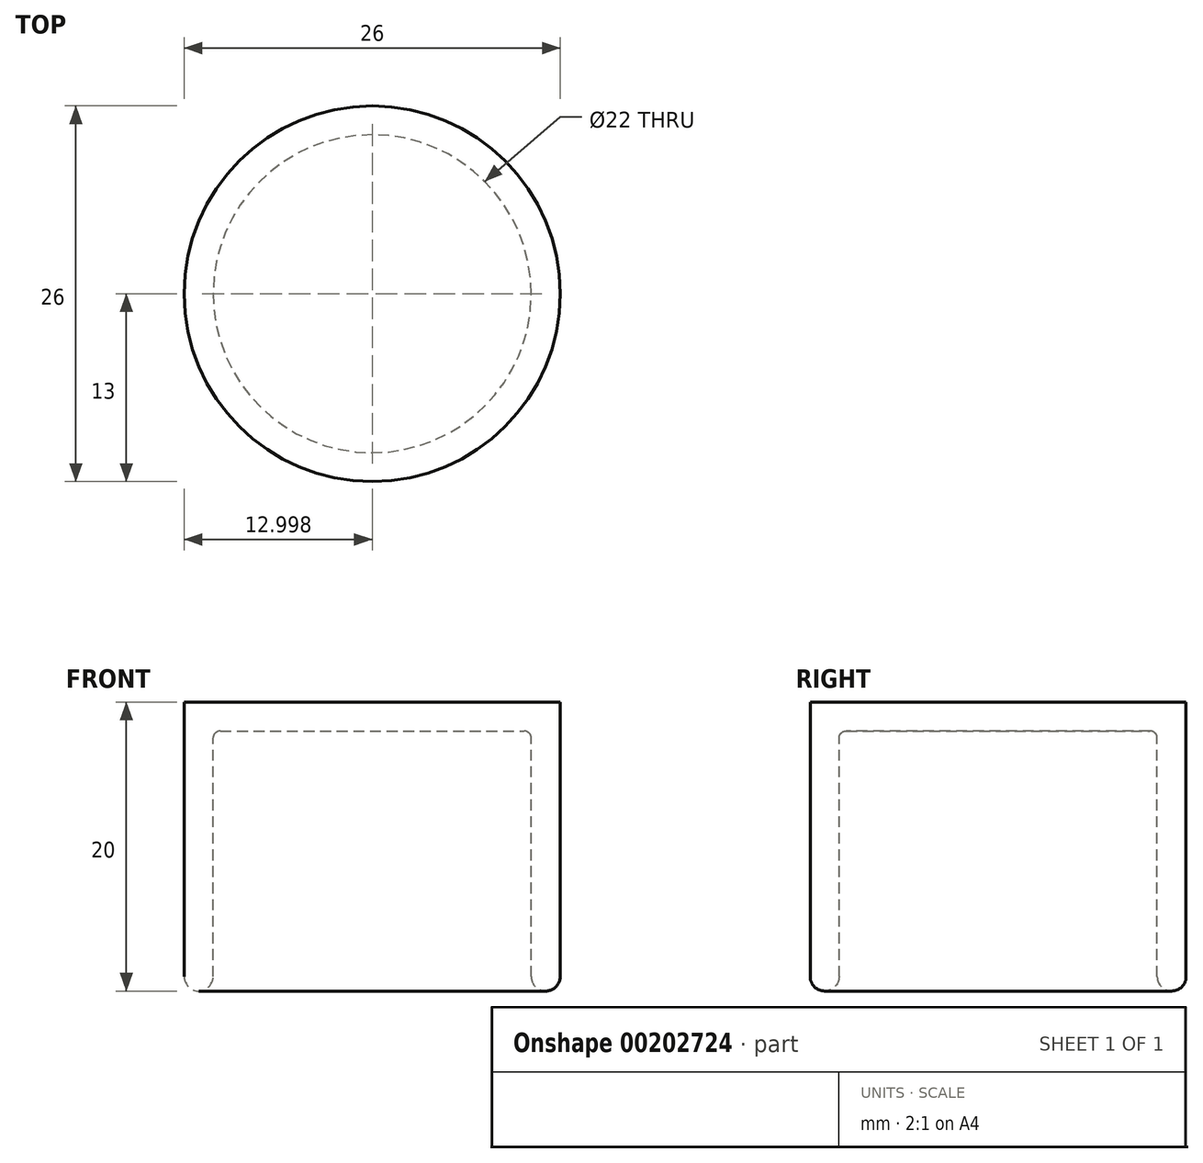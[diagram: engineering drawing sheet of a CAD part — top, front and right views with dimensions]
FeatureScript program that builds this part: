
annotation { "Feature Type Name" : "Feature", "Feature Type Description" : "" }
export const myFeature = defineFeature(function(context is Context, id is Id, definition is map)
    precondition{}
    {
        {
            var Q0;
            Q0=qCreatedBy(makeId("Front.planeOp"),FACE);
            var sketch = newSketch(context, id + "F0", { "sketchPlane" : qUnion([Q0])});
            skLineSegment(sketch, "E0.bottom", {"start": v(18.54, 12.93) * mm, "end": v(31.54, 12.93) * mm});
            skLineSegment(sketch, "E0.top", {"start": v(18.54, -7.07) * mm, "end": v(20.54, -7.07) * mm});
            skLineSegment(sketch, "E0.left", {"start": v(18.54, 12.93) * mm, "end": v(18.54, -7.07) * mm});
            skLineSegment(sketch, "E0.right", {"start": v(31.54, 12.93) * mm, "end": v(31.54, 10.93) * mm});
            skLineSegment(sketch, "E1.0", {"start": v(20.54, 10.93) * mm, "end": v(20.54, -7.07) * mm});
            skLineSegment(sketch, "E1.1", {"start": v(20.54, 10.93) * mm, "end": v(31.54, 10.93) * mm});
            skSolve(sketch);
        }
        {
            var Q0;
            Q0 = qSketchRegion(id + "F0", true);
            var Q1;
            Q1=sQuery(id+"F0.wireOp",EDGE,"E0.right");
            revolve(context, id + "F1", {"entities" : qUnion([Q0]), "axis" : qUnion([Q1]), "revolveType" : RevolveType.FULL});
        }
        {
            var Q0;
            Q0=makeQuery(id+"F1.opRevolve","SWEPT_FACE",FACE,{"disambiguationData":[OSD([sQuery(id+"F0.wireOp",EDGE,"E1.1")])]});
            fillet(context, id + "F2", {"entities" : qUnion([Q0]), "radius" : 0.5 * mm, "tangentPropagation" : true, "allowEdgeOverflow" : false});
        }
        {
            var Q0;
            Q0=makeQuery(id+"F1.opRevolve","SWEPT_FACE",FACE,{"disambiguationData":[OSD([sQuery(id+"F0.wireOp",EDGE,"E0.top")])]});
            fillet(context, id + "F3", {"entities" : qUnion([Q0]), "radius" : 1 * mm, "tangentPropagation" : true, "allowEdgeOverflow" : false});
        }
    });
